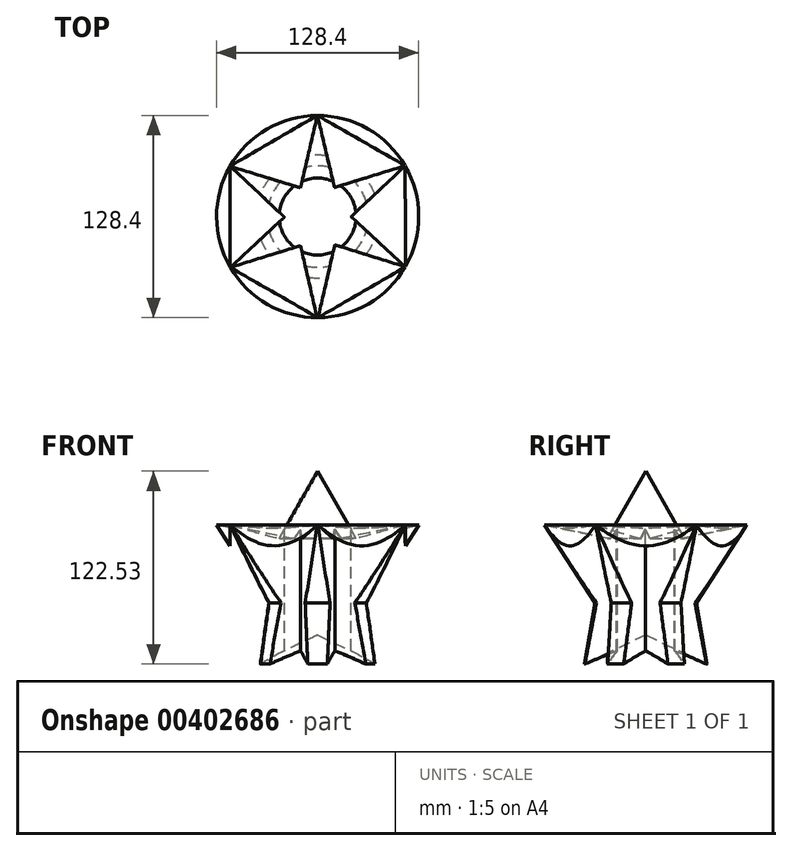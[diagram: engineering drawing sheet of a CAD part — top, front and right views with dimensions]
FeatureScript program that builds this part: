
annotation { "Feature Type Name" : "Feature", "Feature Type Description" : "" }
export const myFeature = defineFeature(function(context is Context, id is Id, definition is map)
    precondition{}
    {
        {
            var Q0;
            Q0=qCreatedBy(makeId("Front.planeOp"),FACE);
            var sketch = newSketch(context, id + "F0", { "sketchPlane" : qUnion([Q0])});
            skArc(sketch, "E0.cCircle", {"start": v(0, 55.5) * mm, "mid": v(-3.91, 55.37) * mm, "end": v(-7.8, 54.95) * mm, "construction": true});
            skPoint(sketch, "E0.0.midPoint", {"position": v(0, -55.5) * mm});
            skLineSegment(sketch, "E1", {"start": v(0, 68.6) * mm, "end": v(0, -55.5) * mm});
            skArc(sketch, "E2", {"start": v(0, 35.58) * mm, "mid": v(-35.58, 0) * mm, "end": v(0, -35.58) * mm});
            skLineSegment(sketch, "E3", {"start": v(0, 68.6) * mm, "end": v(-24.45, 25.86) * mm});
            skLineSegment(sketch, "E4", {"start": v(-24.45, 25.86) * mm, "end": v(-64.2, 34.43) * mm});
            skLineSegment(sketch, "E5", {"start": v(-64.2, 34.43) * mm, "end": v(-32.22, -15.1) * mm});
            skLineSegment(sketch, "E6", {"start": v(-32.22, -15.1) * mm, "end": v(-38.99, -53.92) * mm});
            skLineSegment(sketch, "E7", {"start": v(-38.99, -53.92) * mm, "end": v(0, -35.58) * mm});
            skPoint(sketch, "E8.orphan", {"position": v(38.99, -57.09) * mm});
            skSolve(sketch);
        }
        {
            var Q0;
            Q0 = qSketchRegion(id + "F0", true);
            var Q1;
            Q1=sQuery(id+"F0.wireOp",EDGE,"E1");
            revolve(context, id + "F1", {"entities" : qUnion([Q0]), "axis" : qUnion([Q1]), "revolveType" : RevolveType.FULL});
        }
        {
            var Q0;
            Q0=qCreatedBy(makeId("Top.planeOp"),FACE);
            var sketch = newSketch(context, id + "F2", { "sketchPlane" : qUnion([Q0])});
            skCircle(sketch, "E9.cCircle", {"center": v(0, 0) * mm, "radius": 55.66 * mm, "construction": true});
            skLineSegment(sketch, "E9.0", {"start": v(55.76, -31.96) * mm, "end": v(0.2, -64.27) * mm});
            skLineSegment(sketch, "E9.1", {"start": v(0.2, -64.27) * mm, "end": v(-55.56, -32.3) * mm});
            skLineSegment(sketch, "E9.2", {"start": v(-55.56, -32.3) * mm, "end": v(-55.76, 31.96) * mm});
            skLineSegment(sketch, "E9.3", {"start": v(-55.76, 31.96) * mm, "end": v(-0.2, 64.27) * mm});
            skLineSegment(sketch, "E9.4", {"start": v(-0.2, 64.27) * mm, "end": v(55.56, 32.3) * mm});
            skLineSegment(sketch, "E9.5", {"start": v(55.56, 32.3) * mm, "end": v(55.76, -31.96) * mm});
            skPoint(sketch, "E9.0.midPoint", {"position": v(27.98, -48.12) * mm});
            skCircle(sketch, "E10", {"center": v(0, 0) * mm, "radius": 14.7 * mm});
            skLineSegment(sketch, "E11", {"start": v(-55.76, 31.96) * mm, "end": v(-8.69, -11.85) * mm});
            skLineSegment(sketch, "E12", {"start": v(-55.76, 31.96) * mm, "end": v(7.67, 12.53) * mm});
            skLineSegment(sketch, "E13", {"start": v(-0.2, 64.27) * mm, "end": v(-14.31, 3.31) * mm});
            skLineSegment(sketch, "E14", {"start": v(-0.2, 64.27) * mm, "end": v(15.1, 0) * mm});
            skLineSegment(sketch, "E15", {"start": v(55.56, 32.3) * mm, "end": v(-6.56, 13.14) * mm});
            skLineSegment(sketch, "E16", {"start": v(55.56, 32.3) * mm, "end": v(10.1, -10.68) * mm});
            skLineSegment(sketch, "E17", {"start": v(55.76, -31.96) * mm, "end": v(7.67, 12.53) * mm});
            skLineSegment(sketch, "E18", {"start": v(55.76, -31.96) * mm, "end": v(-8.69, -11.85) * mm});
            skLineSegment(sketch, "E19", {"start": v(0.2, -64.27) * mm, "end": v(13.31, -7.63) * mm});
            skLineSegment(sketch, "E20", {"start": v(0, -65.97) * mm, "end": v(-15.07, 0) * mm});
            skLineSegment(sketch, "E21", {"start": v(-55.56, -32.3) * mm, "end": v(6.8, -13.02) * mm});
            skLineSegment(sketch, "E22", {"start": v(-55.56, -32.3) * mm, "end": v(-6.56, 13.14) * mm});
            skSolve(sketch);
        }
        {
            var Q0;
            {var subQ0=sQuery(id+"F2.wireOp",EDGE,"E9.3");Q0=makeQuery(id+"F2.imprint","IMPRINT",FACE,{"disambiguationData":[TD([[makeQuery(id+"F2.imprint","IMPRINT",EDGE,{"derivedFrom":subQ0}),-1.0]])]});}
            var Q1;
            {var subQ0=sQuery(id+"F2.wireOp",EDGE,"E9.4");Q1=makeQuery(id+"F2.imprint","IMPRINT",FACE,{"disambiguationData":[TD([[makeQuery(id+"F2.imprint","IMPRINT",EDGE,{"derivedFrom":subQ0}),-1.0]])]});}
            var Q2;
            {var subQ0=sQuery(id+"F2.wireOp",EDGE,"E9.5");Q2=makeQuery(id+"F2.imprint","IMPRINT",FACE,{"disambiguationData":[TD([[makeQuery(id+"F2.imprint","IMPRINT",EDGE,{"derivedFrom":subQ0}),-1.0]])]});}
            var Q3;
            {var subQ0=sQuery(id+"F2.wireOp",EDGE,"E9.0");Q3=makeQuery(id+"F2.imprint","IMPRINT",FACE,{"disambiguationData":[TD([[makeQuery(id+"F2.imprint","IMPRINT",EDGE,{"derivedFrom":subQ0}),-1.0]])]});}
            var Q4;
            {var subQ1=sQuery(id+"F2.wireOp",EDGE,"E9.1");var subQ3=sQuery(id+"F2.wireOp",EDGE,"E20");var subQ4=makeQuery(id+"F2.imprint","INTERSECT",VERTEX,{"derivedFrom":[subQ1,subQ3]});Q4=makeQuery(id+"F2.imprint","IMPRINT",FACE,{"disambiguationData":[TD([[makeQuery(id+"F2.imprint","IMPRINT",EDGE,{"disambiguationData":[TD([[subQ4,-1.0]])],"derivedFrom":subQ3}),1.0]])]});}
            var Q5;
            {var subQ0=sQuery(id+"F2.wireOp",EDGE,"E9.2");Q5=makeQuery(id+"F2.imprint","IMPRINT",FACE,{"disambiguationData":[TD([[makeQuery(id+"F2.imprint","IMPRINT",EDGE,{"derivedFrom":subQ0}),-1.0]])]});}
            extrude(context, id + "F3", {"entities" : qUnion([Q0, Q1, Q2, Q3, Q4, Q5]), "operationType" : NewBodyOperationType.REMOVE, "endBound" : BoundingType.SYMMETRIC, "oppositeDirection" : true, "depth" : 112 * mm});
        }
    });
